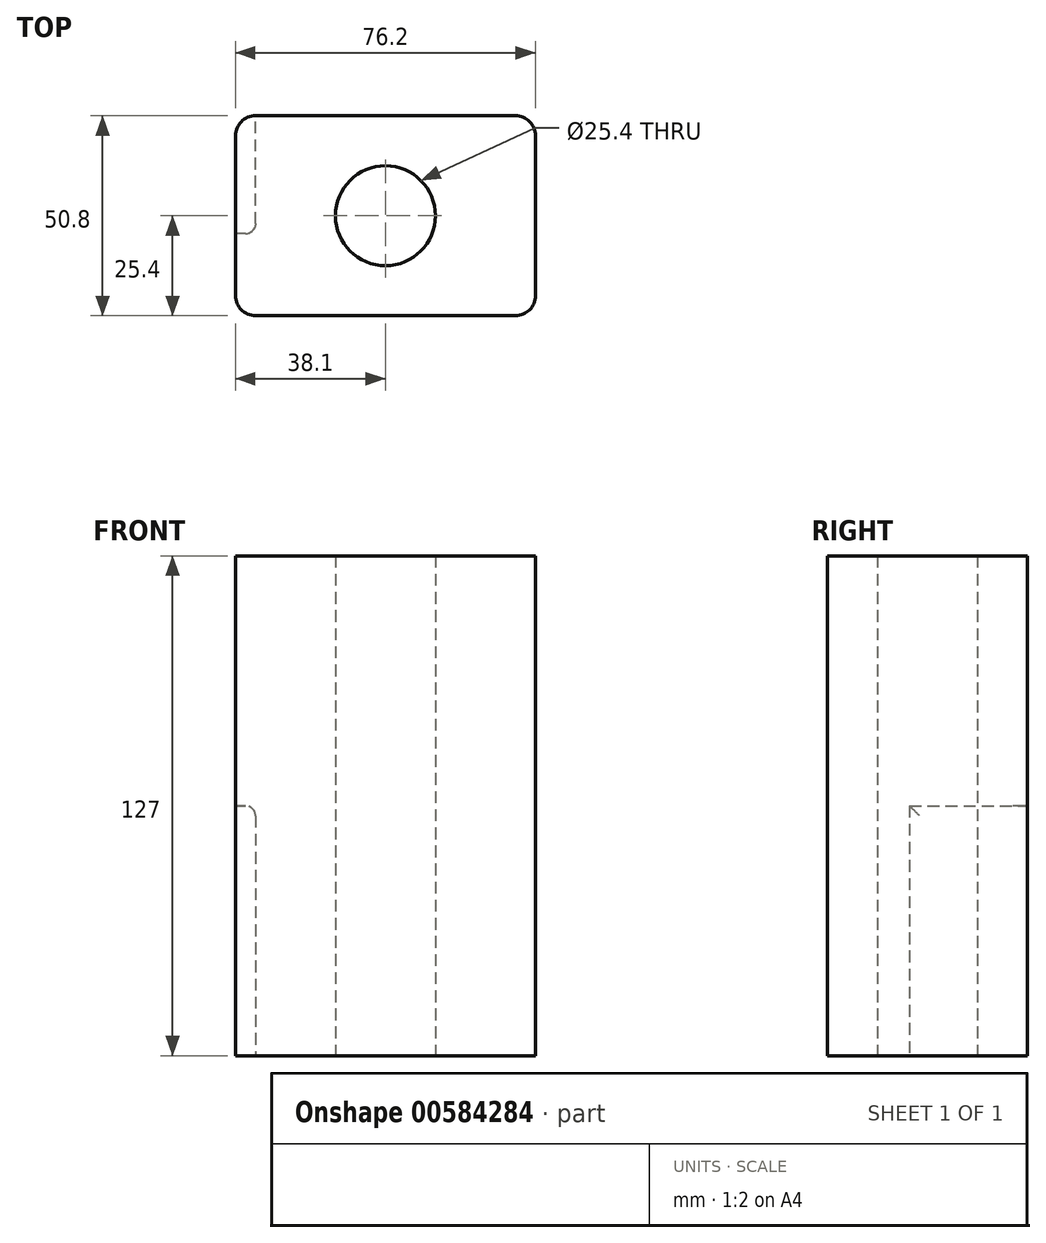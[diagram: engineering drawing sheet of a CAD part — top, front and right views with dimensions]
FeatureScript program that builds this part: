
annotation { "Feature Type Name" : "Feature", "Feature Type Description" : "" }
export const myFeature = defineFeature(function(context is Context, id is Id, definition is map)
    precondition{}
    {
        {
            var Q0;
            Q0=qCreatedBy(makeId("Top.planeOp"),FACE);
            var sketch = newSketch(context, id + "F0", { "sketchPlane" : qUnion([Q0])});
            skLineSegment(sketch, "E0.bottom", {"start": v(-38.1, -25.4) * mm, "end": v(38.1, -25.4) * mm});
            skLineSegment(sketch, "E0.top", {"start": v(-38.1, 25.4) * mm, "end": v(38.1, 25.4) * mm});
            skLineSegment(sketch, "E0.left", {"start": v(-38.1, -25.4) * mm, "end": v(-38.1, 25.4) * mm});
            skLineSegment(sketch, "E0.right", {"start": v(38.1, -25.4) * mm, "end": v(38.1, 25.4) * mm});
            skPoint(sketch, "E0.middle", {"position": v(0, 0) * mm});
            skCircle(sketch, "E1", {"center": v(0, 0) * mm, "radius": 12.7 * mm});
            skSolve(sketch);
        }
        {
            var Q0;
            Q0 = qSketchRegion(id + "F0", true);
            extrude(context, id + "F1", {"entities" : qUnion([Q0]), "endBound" : BoundingType.SYMMETRIC, "depth" : 127 * mm, "offsetDistance" : 25.4 * mm});
        }
        {
            var Q0;
            Q0=makeQuery(id+"F1.opExtrude","SWEPT_EDGE",EDGE,{"disambiguationData":[OSD([sQuery(id+"F0.wireOp",EDGE,"E0.top"),sQuery(id+"F0.wireOp",EDGE,"E0.right")])]});
            var Q1;
            Q1=makeQuery(id+"F1.opExtrude","SWEPT_EDGE",EDGE,{"disambiguationData":[OSD([sQuery(id+"F0.wireOp",EDGE,"E0.bottom"),sQuery(id+"F0.wireOp",EDGE,"E0.right")])]});
            var Q2;
            Q2=makeQuery(id+"F1.opExtrude","SWEPT_EDGE",EDGE,{"disambiguationData":[OSD([sQuery(id+"F0.wireOp",EDGE,"E0.bottom"),sQuery(id+"F0.wireOp",EDGE,"E0.left")])]});
            var Q3;
            Q3=makeQuery(id+"F1.opExtrude","SWEPT_EDGE",EDGE,{"disambiguationData":[OSD([sQuery(id+"F0.wireOp",EDGE,"E0.top"),sQuery(id+"F0.wireOp",EDGE,"E0.left")])]});
            fillet(context, id + "F2", {"entities" : qUnion([Q0, Q1, Q2, Q3]), "radius" : 5.08 * mm, "tangentPropagation" : true, "allowEdgeOverflow" : false});
        }
        {
            var Q0;
            Q0=makeQuery(id+"F1.opExtrude","SWEPT_FACE",FACE,{"disambiguationData":[OSD([sQuery(id+"F0.wireOp",EDGE,"E0.top")])]});
            var sketch = newSketch(context, id + "F3", { "sketchPlane" : qUnion([Q0])});
            skLineSegment(sketch, "E2.bottom", {"start": v(58.06, 0) * mm, "end": v(13.6, 0) * mm});
            skLineSegment(sketch, "E2.top", {"start": v(58.06, -127) * mm, "end": v(7.26, -127) * mm});
            skLineSegment(sketch, "E2.left", {"start": v(58.06, 0) * mm, "end": v(58.06, -127) * mm});
            skLineSegment(sketch, "E2.right", {"start": v(7.26, -6.35) * mm, "end": v(7.26, -127) * mm});
            skPoint(sketch, "E3.visualSharp", {"position": v(7.26, 0) * mm});
            skArc(sketch, "E3.filletArc", {"start": v(13.6, 0) * mm, "mid": v(9.12, -1.86) * mm, "end": v(7.26, -6.35) * mm});
            skSolve(sketch);
        }
        {
            var Q0;
            {var subQ1=sQuery(id+"F3.wireOp",EDGE,"E2.top");Q0=makeQuery(id+"F3.imprint","IMPRINT",FACE,{"disambiguationData":[TD([[makeQuery(id+"F3.imprint","IMPRINT",EDGE,{"derivedFrom":subQ1}),-1.0]])]});}
            extrude(context, id + "F4", {"entities" : qUnion([Q0]), "operationType" : NewBodyOperationType.REMOVE, "oppositeDirection" : true, "depth" : 29.97 * mm, "offsetDistance" : 25.4 * mm});
        }
        {
            var Q0;
            Q0=makeQuery(id+"F4.boolean.opBoolean","COPY",EDGE,{"derivedFrom":makeQuery(id+"F4.opExtrude","SWEPT_EDGE",EDGE,{"disambiguationData":[OSD([sQuery(id+"F0.wireOp",EDGE,"E0.top"),sQuery(id+"F0.wireOp",EDGE,"E0.left"),sQuery(id+"F3.wireOp",EDGE,"E2.bottom")])]})});
            var Q1;
            Q1=makeQuery(id+"F4.boolean.opBoolean","COPY",EDGE,{"derivedFrom":makeQuery(id+"F4.opExtrude","CAP_EDGE",EDGE,{"disambiguationData":[OSD([sQuery(id+"F0.wireOp",EDGE,"E0.top"),sQuery(id+"F0.wireOp",EDGE,"E0.left")])],"isStart":false})});
            fillet(context, id + "F5", {"entities" : qUnion([Q0, Q1]), "radius" : 2.54 * mm, "tangentPropagation" : true, "allowEdgeOverflow" : false});
        }
    });
